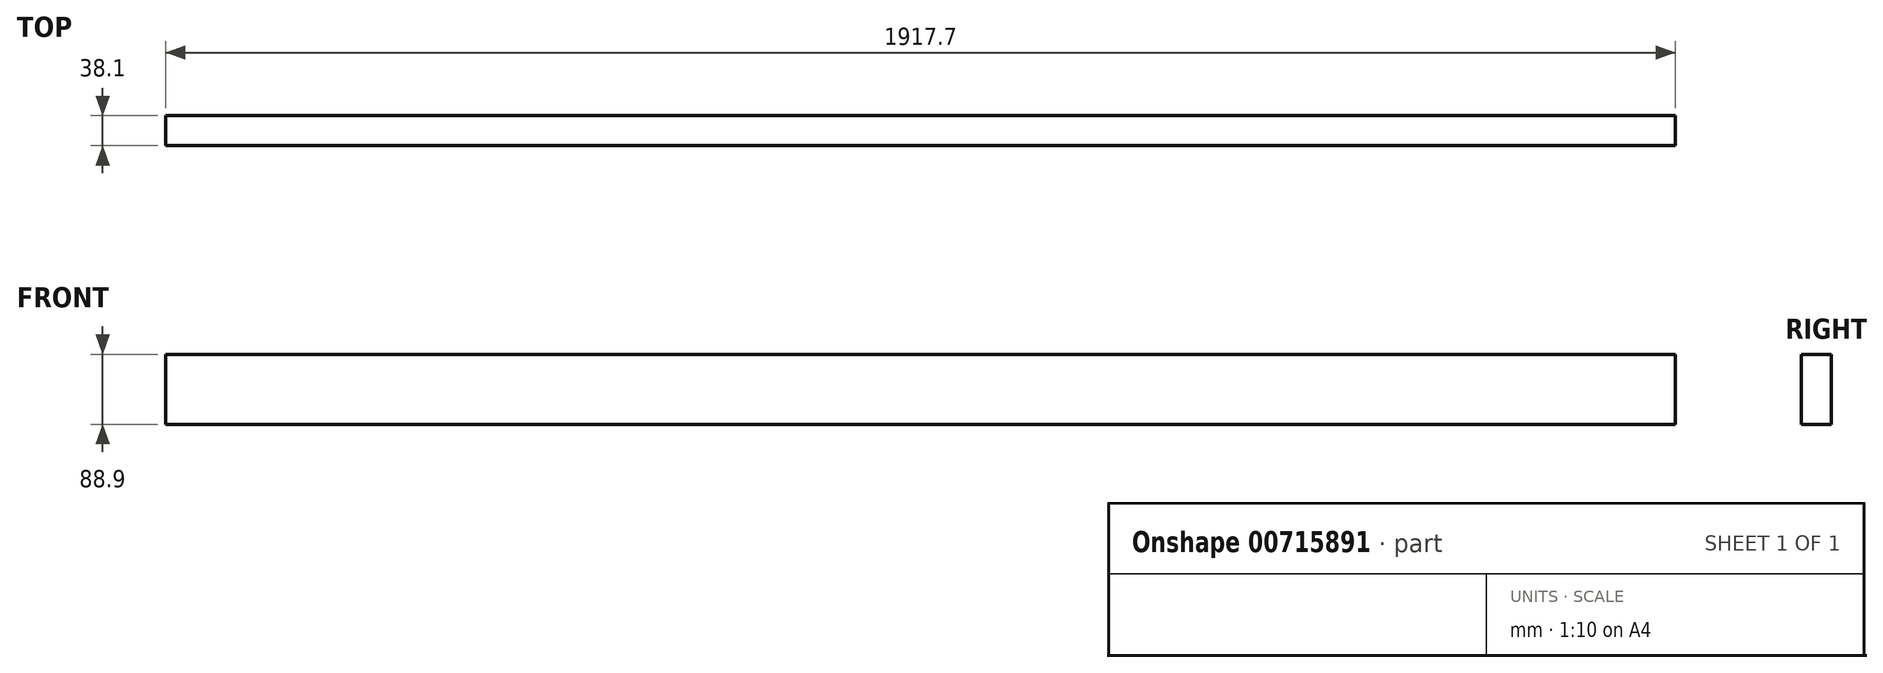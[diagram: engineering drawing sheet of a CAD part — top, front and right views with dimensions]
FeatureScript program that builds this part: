
annotation { "Feature Type Name" : "Feature", "Feature Type Description" : "" }
export const myFeature = defineFeature(function(context is Context, id is Id, definition is map)
    precondition{}
    {
        {
            var Q0;
            Q0=qCreatedBy(makeId("Right.planeOp"),FACE);
            var sketch = newSketch(context, id + "F0", { "sketchPlane" : qUnion([Q0])});
            skLineSegment(sketch, "E0.bottom", {"start": v(-19.05, 44.45) * mm, "end": v(19.05, 44.45) * mm});
            skLineSegment(sketch, "E0.top", {"start": v(-19.05, -44.45) * mm, "end": v(19.05, -44.45) * mm});
            skLineSegment(sketch, "E0.left", {"start": v(-19.05, 44.45) * mm, "end": v(-19.05, -44.45) * mm});
            skLineSegment(sketch, "E0.right", {"start": v(19.05, 44.45) * mm, "end": v(19.05, -44.45) * mm});
            skPoint(sketch, "E0.middle", {"position": v(0, 0) * mm});
            skSolve(sketch);
        }
        {
            var Q0;
            Q0=qSketchRegion(id+"F0",true);
            extrude(context, id + "F1", {"entities" : qUnion([Q0]), "depth" : 1917.7 * mm, "offsetDistance" : 25.4 * mm, "symmetric" : true});
        }
    });
